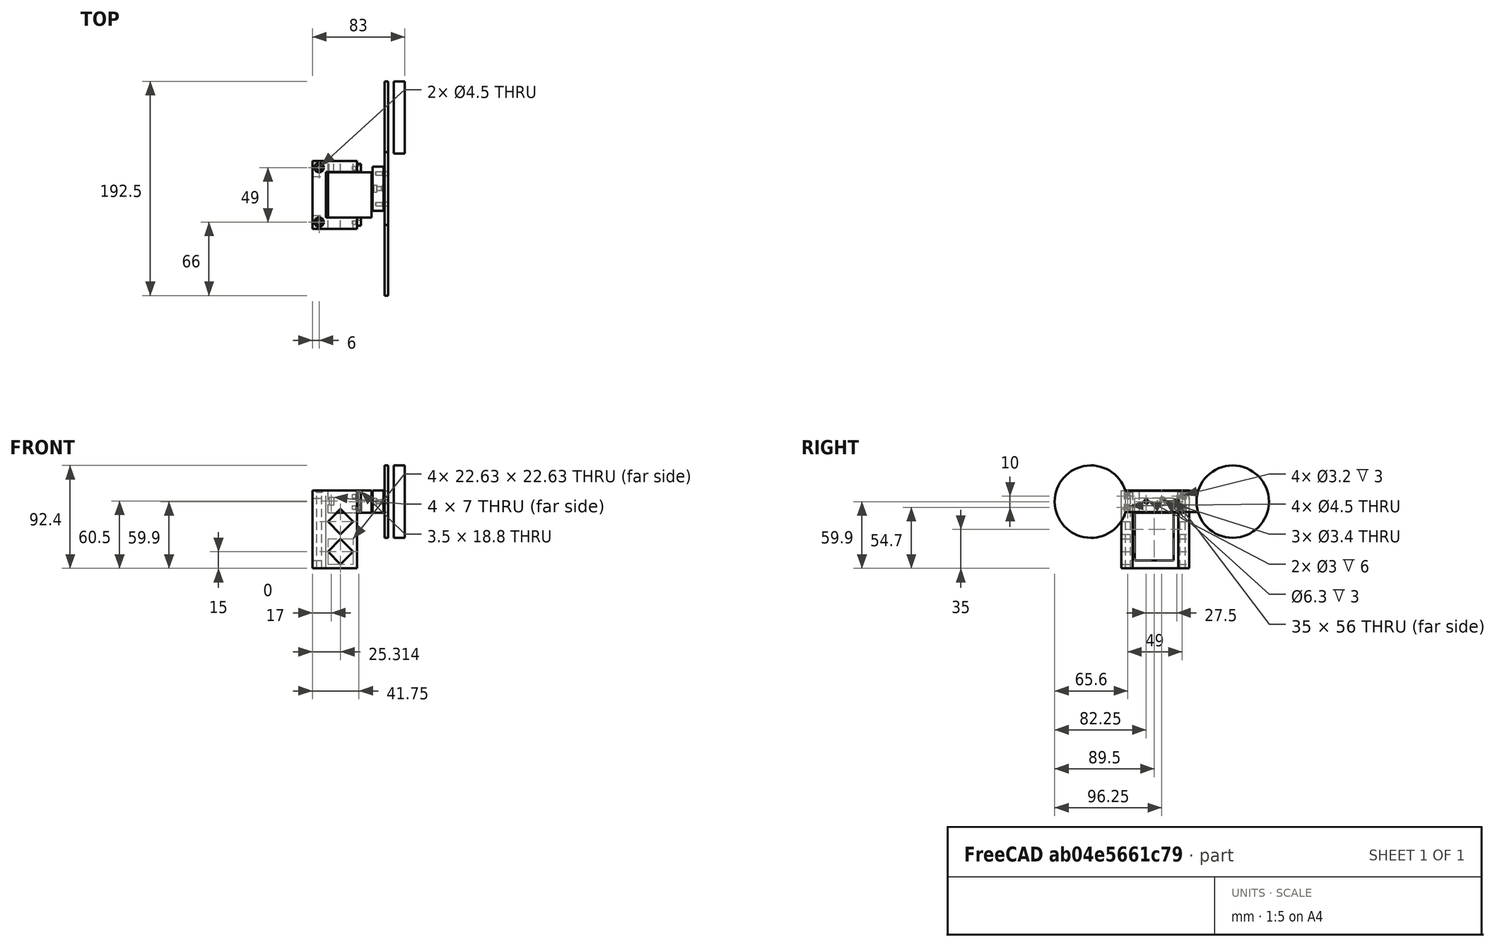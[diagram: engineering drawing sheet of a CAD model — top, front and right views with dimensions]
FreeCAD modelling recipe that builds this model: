
FCSTD DOCUMENT  (FreeCAD 0.19R24276 (Git))
Label: Projector Servo switch
License: All rights reserved
LicenseURL: http://en.wikipedia.org/wiki/All_rights_reserved
objects: Part::Cylinder×20, Part::Box×13, Part::Cut×12, Part::MultiFuse×11, Part::Chamfer×5, Part::Fuse×1, Part::Feature×1
note: 63 computed .brp shape members not serialized (recipe doc carries the construction recipe); baked Part::Feature solids carry a one-line shape summary decoded from their .brp

FEATURE [Part::Box] Box  label="Cube"
  AttacherType = Attacher::AttachEngine3D
  Height = 70
  Length = 40
  Width = 61
FEATURE [Part::Box] Box001  label="Cube001"
  AttacherType = Attacher::AttachEngine3D
  Height = 75
  Length = 28
  Placement = pos=(12,10,0) rot=(0,0,1;0rad)
  Width = 41
FEATURE [Part::Cut] Cut
  Base = -> Box
  Tool = -> Box001
FEATURE [Part::Box] Box002  label="Cube002"
  AttacherType = Attacher::AttachEngine3D
  Height = 19.8
  Length = 39
  Placement = pos=(14,10.25,50) rot=(0,0,1;0rad)
  Width = 40.5
FEATURE [Part::Box] Box003  label="Cube003"
  AttacherType = Attacher::AttachEngine3D
  Height = 18.8
  Length = 3.5
  Placement = pos=(40,2.75,50.5) rot=(0,0,1;0rad)
  Width = 7.5
FEATURE [Part::Box] Box004  label="Cube004"
  AttacherType = Attacher::AttachEngine3D
  Height = 18.8
  Length = 3.5
  Placement = pos=(40,50.75,50.5) rot=(0,0,1;0rad)
  Width = 7.5
FEATURE [Part::Cylinder] Cylinder
  Angle = 360
  AttacherType = Attacher::AttachEngine3D
  Height = 10
  Placement = pos=(36,5.6,64.7) rot=(0,1,0;1.5708rad)
  Radius = 2.25
FEATURE [Part::Cylinder] Cylinder001
  Angle = 360
  AttacherType = Attacher::AttachEngine3D
  Height = 10
  Placement = pos=(36,5.6,54.7) rot=(0,1,0;1.5708rad)
  Radius = 2.25
FEATURE [Part::Cylinder] Cylinder002
  Angle = 360
  AttacherType = Attacher::AttachEngine3D
  Height = 10
  Placement = pos=(36,54.6,64.7) rot=(0,1,0;1.5708rad)
  Radius = 2.25
FEATURE [Part::Cylinder] Cylinder003
  Angle = 360
  AttacherType = Attacher::AttachEngine3D
  Height = 10
  Placement = pos=(36,54.6,54.7) rot=(0,1,0;1.5708rad)
  Radius = 2.25
FEATURE [Part::Cylinder] Cylinder004
  Angle = 360
  AttacherType = Attacher::AttachEngine3D
  Height = 10
  Placement = pos=(45,36.25,59.9) rot=(0,1,0;1.5708rad)
  Radius = 2
FEATURE [Part::MultiFuse] Fusion
  Shapes = -> [Cylinder001,Cylinder]
FEATURE [Part::MultiFuse] Fusion001
  Shapes = -> [Cylinder002,Cylinder003]
FEATURE [Part::MultiFuse] Fusion002
  Shapes = -> [Box002,Box003,Box004]
FEATURE [Part::MultiFuse] Fusion003
  Shapes = -> [Fusion001,Fusion]
FEATURE [Part::Cut] Cut001
  Base = -> Fusion002
  Tool = -> Fusion003
FEATURE [Part::Cylinder] Cylinder005
  Angle = 360
  AttacherType = Attacher::AttachEngine3D
  Height = 10
  Placement = pos=(36,54.6,64.7) rot=(0,1,0;1.5708rad)
  Radius = 1.6
FEATURE [Part::Cylinder] Cylinder006
  Angle = 360
  AttacherType = Attacher::AttachEngine3D
  Height = 10
  Placement = pos=(36,54.6,54.7) rot=(0,1,0;1.5708rad)
  Radius = 1.6
FEATURE [Part::Cylinder] Cylinder007
  Angle = 360
  AttacherType = Attacher::AttachEngine3D
  Height = 10
  Placement = pos=(36,5.6,64.7) rot=(0,1,0;1.5708rad)
  Radius = 1.6
FEATURE [Part::Cylinder] Cylinder008
  Angle = 360
  AttacherType = Attacher::AttachEngine3D
  Height = 10
  Placement = pos=(36,5.6,54.7) rot=(0,1,0;1.5708rad)
  Radius = 1.6
FEATURE [Part::Box] Box005  label="Cube005"
  AttacherType = Attacher::AttachEngine3D
  Height = 7
  Length = 4
  Placement = pos=(15,49,57) rot=(0,0,1;0rad)
  Width = 16
FEATURE [Part::Fuse] Fusion004
  Base = -> Cylinder004
  Tool = -> Cut001
FEATURE [Part::MultiFuse] Fusion005
  Shapes = -> [Cylinder005,Cylinder006,Cylinder007,Cylinder008]
FEATURE [Part::Cut] Cut002
  Base = -> Cut
  Tool = -> Fusion005
FEATURE [Part::Cut] Cut003
  Base = -> Cut002
  Tool = -> Box005
FEATURE [Part::Cylinder] Cylinder009
  Angle = 360
  AttacherType = Attacher::AttachEngine3D
  Height = 74
  Placement = pos=(6,6,-2) rot=(0,0,1;0rad)
  Radius = 2.25
FEATURE [Part::Cylinder] Cylinder010
  Angle = 360
  AttacherType = Attacher::AttachEngine3D
  Height = 74
  Placement = pos=(6,55,-2) rot=(0,0,1;0rad)
  Radius = 2.25
FEATURE [Part::MultiFuse] Fusion006
  Shapes = -> [Cylinder009,Cylinder010]
FEATURE [Part::Cut] Cut004
  Base = -> Cut003
  Tool = -> Fusion006
FEATURE [Part::Chamfer] Chamfer
  Base = -> Cut004
  Edges = 2 edges r=2: [Edge14,Edge15]
FEATURE [Part::Box] Box006  label="Cube006"
  AttacherType = Attacher::AttachEngine3D
  Height = 20
  Length = 10
  Placement = pos=(54,16,50) rot=(0,0,1;0rad)
  Width = 40
FEATURE [Part::Cylinder] Cylinder011
  Angle = 360
  AttacherType = Attacher::AttachEngine3D
  Height = 10
  Placement = pos=(48,36.25,59.9) rot=(0,1,0;1.5708rad)
  Radius = 3.15
FEATURE [Part::Cut] Cut005
  Base = -> Box006
  Tool = -> Cylinder011
FEATURE [Part::Cylinder] Cylinder012
  Angle = 360
  AttacherType = Attacher::AttachEngine3D
  Height = 10
  Placement = pos=(57,36.25,59.9) rot=(0,1,0;1.5708rad)
  Radius = 1.7
FEATURE [Part::Cut] Cut006
  Base = -> Cut005
  Tool = -> Cylinder012
FEATURE [Part::Chamfer] Chamfer001
  Base = -> Cut006
  Edges = 1 edges r=2: [Edge16]
FEATURE [Part::Cylinder] Cylinder013
  Angle = 360
  AttacherType = Attacher::AttachEngine3D
  Height = 10
  Placement = pos=(57,49.75,59.9) rot=(0,1,0;1.5708rad)
  Radius = 1.5
FEATURE [Part::Cylinder] Cylinder014
  Angle = 360
  AttacherType = Attacher::AttachEngine3D
  Height = 10
  Placement = pos=(57,22.25,59.9) rot=(0,1,0;1.5708rad)
  Radius = 1.5
FEATURE [Part::MultiFuse] Fusion007
  Shapes = -> [Cylinder013,Cylinder014]
FEATURE [Part::Cut] Cut007
  Base = -> Chamfer001
  Tool = -> Fusion007
FEATURE [Part::Chamfer] Chamfer002
  Base = -> Cut007
  Edges = 2 edges r=1: [Edge5,Edge7]
FEATURE [Part::Box] Box007  label="Cube007"
  AttacherType = Attacher::AttachEngine3D
  Height = 19
  Length = 3
  Placement = pos=(65,-44,50.5) rot=(0,0,1;0rad)
  Width = 159
FEATURE [Part::Cylinder] Cylinder015
  Angle = 360
  AttacherType = Attacher::AttachEngine3D
  Height = 10
  Placement = pos=(73,100,59.9) rot=(0,1,0;1.5708rad)
  Radius = 32.5
FEATURE [Part::Cylinder] Cylinder016
  Angle = 360
  AttacherType = Attacher::AttachEngine3D
  Height = 3
  Placement = pos=(65,100,59.9) rot=(0,1,0;1.5708rad)
  Radius = 32.5
FEATURE [Part::Cylinder] Cylinder017
  Angle = 360
  AttacherType = Attacher::AttachEngine3D
  Height = 3
  Placement = pos=(65,-27.5,59.9) rot=(0,1,0;1.5708rad)
  Radius = 32.5
FEATURE [Part::Cylinder] Cylinder018
  Angle = 360
  AttacherType = Attacher::AttachEngine3D
  Height = 10
  Placement = pos=(62,22.25,59.9) rot=(0,1,0;1.5708rad)
  Radius = 1.7
FEATURE [Part::Cylinder] Cylinder019
  Angle = 360
  AttacherType = Attacher::AttachEngine3D
  Height = 10
  Placement = pos=(60,49.75,59.9) rot=(0,1,0;1.5708rad)
  Radius = 1.7
FEATURE [Part::MultiFuse] Fusion008
  Shapes = -> [Box007,Cylinder016,Cylinder017]
FEATURE [Part::MultiFuse] Fusion009
  Shapes = -> [Cylinder019,Cylinder018]
FEATURE [Part::Cut] Cut008
  Base = -> Fusion008
  Tool = -> Fusion009
FEATURE [Part::Feature] Cut008_cs
  Placement = pos=(0,0,0) rot=(0,1,0;1.5708rad)
  shape: bbox 65 x 192.5 x 3e-07 mm, 0 faces, 0 solids (baked)
FEATURE [Part::Chamfer] Chamfer003
  Base = -> Chamfer002
  Edges = 1 edges r=1: [Edge24]
FEATURE [Part::Chamfer] Chamfer004
  Base = -> Chamfer
  Edges = 4 edges r=1: [Edge22,Edge23,Edge38,Edge39]
FEATURE [Part::Box] Box008  label="Cube008"
  AttacherType = Attacher::AttachEngine3D
  Height = 56
  Length = 15
  Placement = pos=(-1,12,7) rot=(0,0,1;0rad)
  Width = 35
FEATURE [Part::Cut] Cut009
  Base = -> Chamfer004
  Tool = -> Box008
FEATURE [Part::Box] Box009  label="Cube009"
  AttacherType = Attacher::AttachEngine3D
  Height = 16
  Length = 16
  Placement = pos=(14,-1,15) rot=(0,1,0;0.785398rad)
  Width = 12
FEATURE [Part::Box] Box010  label="Cube010"
  AttacherType = Attacher::AttachEngine3D
  Height = 16
  Length = 16
  Placement = pos=(14,-1,42) rot=(0,1,0;0.785398rad)
  Width = 12
FEATURE [Part::MultiFuse] Fusion010
  Shapes = -> [Box009,Box010]
FEATURE [Part::Cut] Cut010
  Base = -> Cut009
  Tool = -> Fusion010
FEATURE [Part::Box] Box011  label="Cube011"
  AttacherType = Attacher::AttachEngine3D
  Height = 16
  Length = 16
  Placement = pos=(14,50,15) rot=(0,1,0;0.785398rad)
  Width = 12
FEATURE [Part::Box] Box012  label="Cube012"
  AttacherType = Attacher::AttachEngine3D
  Height = 16
  Length = 16
  Placement = pos=(14,50,42) rot=(0,1,0;0.785398rad)
  Width = 12
FEATURE [Part::MultiFuse] Fusion011
  Shapes = -> [Box011,Box012]
FEATURE [Part::Cut] Cut011
  Base = -> Cut010
  Tool = -> Fusion011
